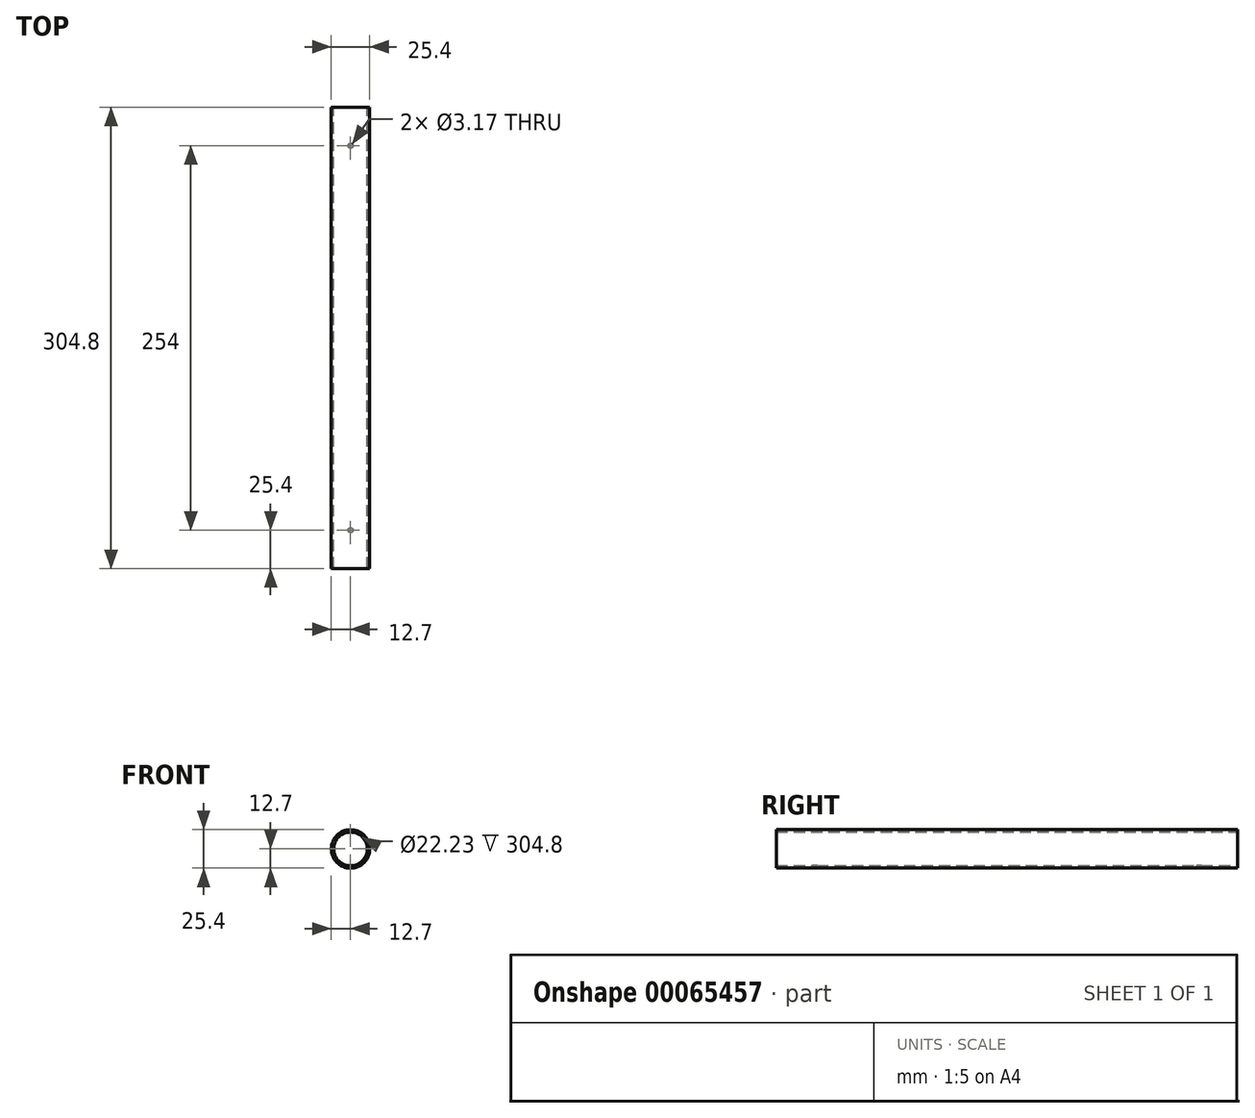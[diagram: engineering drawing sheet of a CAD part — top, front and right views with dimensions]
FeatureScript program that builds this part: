
annotation { "Feature Type Name" : "Feature", "Feature Type Description" : "" }
export const myFeature = defineFeature(function(context is Context, id is Id, definition is map)
    precondition{}
    {
        {
            var Q0;
            Q0=qCreatedBy(makeId("Front.planeOp"),FACE);
            var sketch = newSketch(context, id + "F0", { "sketchPlane" : qUnion([Q0])});
            skCircle(sketch, "E0", {"center": v(0, 0) * mm, "radius": 12.7 * mm});
            skCircle(sketch, "E1", {"center": v(0, 0) * mm, "radius": 11.11 * mm});
            skSolve(sketch);
        }
        {
            var Q0;
            Q0=makeQuery(id+"F0.imprint","IMPRINT",FACE,{"disambiguationData":[TD([[makeQuery(id+"F0.imprint","IMPRINT",EDGE,{"derivedFrom":sQuery(id+"F0.wireOp",EDGE,"E0")}),1.0]])]});
            extrude(context, id + "F1", {"entities" : qUnion([Q0]), "depth" : 304.8 * mm});
        }
        {
            var Q0;
            Q0=qCreatedBy(makeId("Top.planeOp"),FACE);
            var sketch = newSketch(context, id + "F2", { "sketchPlane" : qUnion([Q0])});
            skLineSegment(sketch, "E2", {"start": v(0, 0) * mm, "end": v(0, -25.4) * mm});
            skLineSegment(sketch, "E3", {"start": v(0, -25.4) * mm, "end": v(0, -279.4) * mm});
            skSolve(sketch);
        }
        {
            var Q0;
            Q0=sQuery(id+"F2.wireOp",VERTEX,"E3.end");
            var Q1;
            Q1=sQuery(id+"F2.wireOp",VERTEX,"E3.start");
            var Q2;
            Q2=makeQuery(id+"F1.opExtrude","SWEPT_BODY",BODY,{"disambiguationData":[OSD([sQuery(id+"F0.wireOp",EDGE,"E0"),sQuery(id+"F0.wireOp",EDGE,"E1")])]});
            hole(context, id + "F3", {"style" : HoleStyle.SIMPLE, "holeDiameter" : 3.17 * mm, "endStyle" : HoleEndStyle.THROUGH, "locations" : qUnion([Q0, Q1]), "scope" : qUnion([Q2])});
        }
    });
